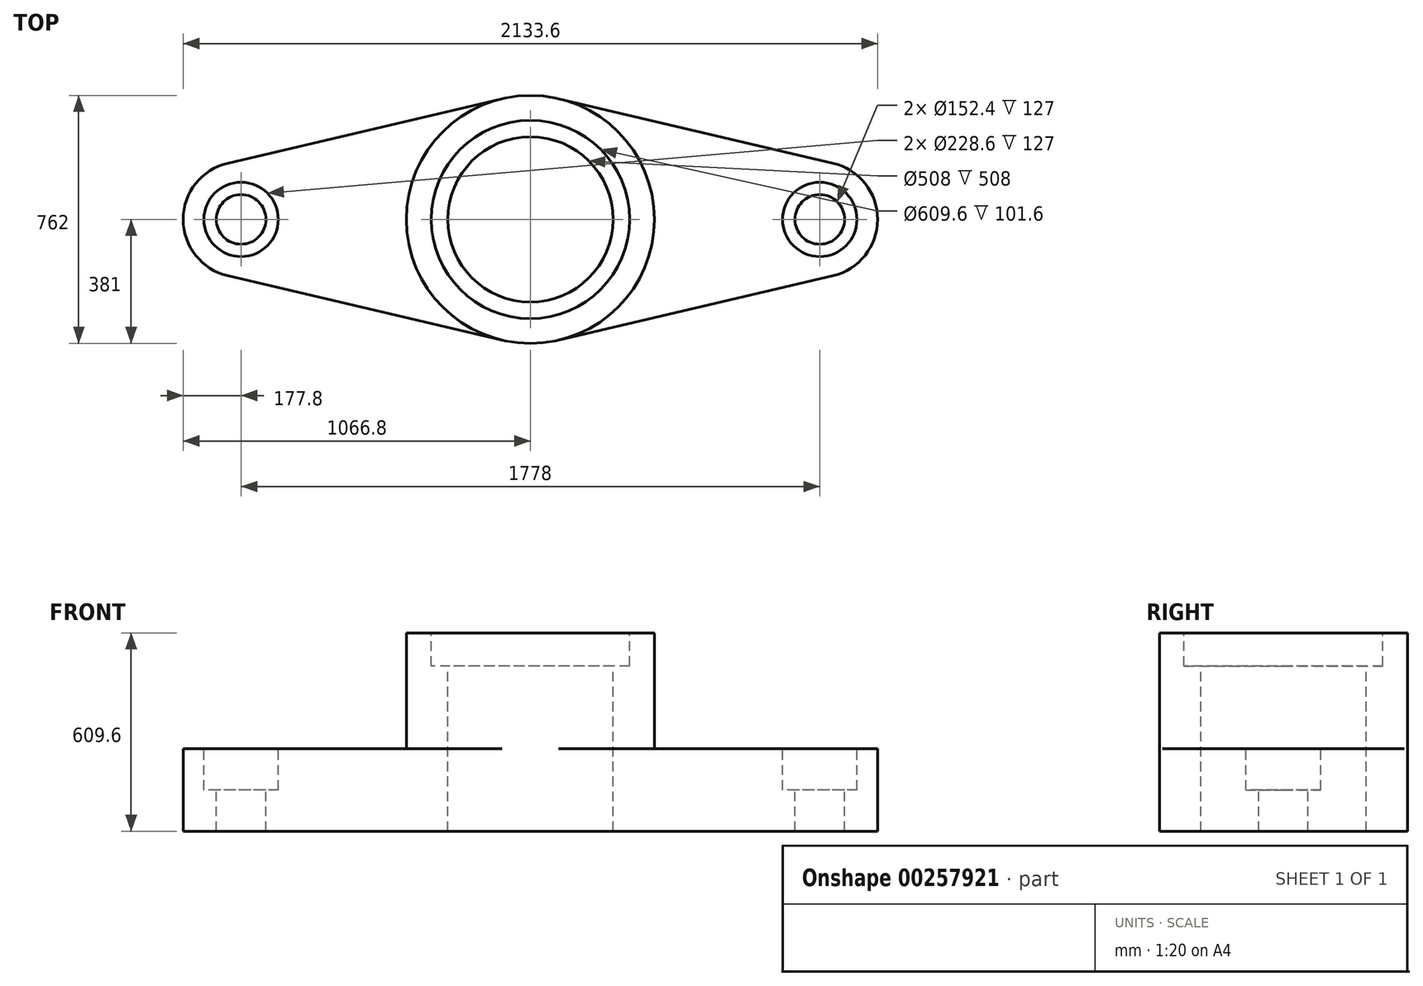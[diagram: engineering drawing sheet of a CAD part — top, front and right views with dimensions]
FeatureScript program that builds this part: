
annotation { "Feature Type Name" : "Feature", "Feature Type Description" : "" }
export const myFeature = defineFeature(function(context is Context, id is Id, definition is map)
    precondition{}
    {
        {
            var Q0;
            Q0=qCreatedBy(makeId("Top.planeOp"),FACE);
            var sketch = newSketch(context, id + "F0", { "sketchPlane" : qUnion([Q0])});
            skCircle(sketch, "E0", {"center": v(0, 0) * mm, "radius": 381 * mm});
            skLineSegment(sketch, "E1", {"start": v(-658.77, 0) * mm, "end": v(889.36, 0) * mm, "construction": true});
            skArc(sketch, "E2", {"start": v(-929.64, 173.1) * mm, "mid": v(-1066.8, 0) * mm, "end": v(-929.64, -173.1) * mm});
            skLineSegment(sketch, "E3", {"start": v(0, 868.24) * mm, "end": v(0, -595.44) * mm, "construction": true});
            skArc(sketch, "E4.MirrorC", {"start": v(929.64, 173.1) * mm, "mid": v(1066.8, 0) * mm, "end": v(929.64, -173.1) * mm});
            skLineSegment(sketch, "E5", {"start": v(-87.09, -370.91) * mm, "end": v(-929.64, -173.1) * mm});
            skLineSegment(sketch, "E6", {"start": v(-87.09, 370.91) * mm, "end": v(-929.64, 173.1) * mm});
            skLineSegment(sketch, "E7.MirrorCS", {"start": v(87.09, 370.91) * mm, "end": v(929.64, 173.1) * mm});
            skLineSegment(sketch, "E8.MirrorCS", {"start": v(87.09, -370.91) * mm, "end": v(929.64, -173.1) * mm});
            skSolve(sketch);
        }
        {
            var Q0;
            Q0 = qSketchRegion(id + "F0", true);
            extrude(context, id + "F1", {"entities" : qUnion([Q0]), "oppositeDirection" : true, "depth" : 254 * mm});
        }
        {
            var Q0;
            Q0=makeQuery(id+"F1.opExtrude","CAP_FACE",FACE,{"disambiguationData":[OSD([sQuery(id+"F0.wireOp",EDGE,"E0"),sQuery(id+"F0.wireOp",EDGE,"E2"),sQuery(id+"F0.wireOp",EDGE,"E5"),sQuery(id+"F0.wireOp",EDGE,"E6"),sQuery(id+"F0.wireOp",EDGE,"E7.MirrorCS"),sQuery(id+"F0.wireOp",EDGE,"E4.MirrorC"),sQuery(id+"F0.wireOp",EDGE,"E8.MirrorCS")])],"isStart":true});
            var sketch = newSketch(context, id + "F2", { "sketchPlane" : qUnion([Q0])});
            skCircle(sketch, "E9", {"center": v(0, 0) * mm, "radius": 381 * mm});
            skSolve(sketch);
        }
        {
            var Q0;
            Q0 = qSketchRegion(id + "F2", true);
            extrude(context, id + "F3", {"entities" : qUnion([Q0]), "operationType" : NewBodyOperationType.ADD, "depth" : 355.6 * mm});
        }
        {
            var Q0;
            {var subQ0=sQuery(id+"F0.wireOp",EDGE,"E5");var subQ1=sQuery(id+"F0.wireOp",EDGE,"E2");var subQ2=sQuery(id+"F0.wireOp",EDGE,"E0");var subQ3=sQuery(id+"F0.wireOp",EDGE,"E8.MirrorCS");var subQ4=sQuery(id+"F0.wireOp",EDGE,"E6");var subQ5=sQuery(id+"F0.wireOp",EDGE,"E7.MirrorCS");Q0=makeQuery(id+"F3.boolean.opBoolean","SPLIT",FACE,{"disambiguationData":[TD([makeQuery(id+"F1.opExtrude","SWEPT_FACE",FACE,{"disambiguationData":[OSD([subQ1])]})])],"derivedFrom":makeQuery(id+"F1.opExtrude","CAP_FACE",FACE,{"disambiguationData":[OSD([subQ2,subQ1,subQ0,subQ4,subQ5,sQuery(id+"F0.wireOp",EDGE,"E4.MirrorC"),subQ3])],"isStart":true})});}
            var sketch = newSketch(context, id + "F4", { "sketchPlane" : qUnion([Q0])});
            skCircle(sketch, "E10", {"center": v(-889, 0) * mm, "radius": 76.2 * mm});
            skSolve(sketch);
        }
        {
            var Q0;
            Q0 = qSketchRegion(id + "F4", true);
            extrude(context, id + "F5", {"entities" : qUnion([Q0]), "operationType" : NewBodyOperationType.REMOVE, "oppositeDirection" : true, "depth" : 254 * mm});
        }
        {
            var Q0;
            {var subQ0=sQuery(id+"F0.wireOp",EDGE,"E7.MirrorCS");var subQ1=sQuery(id+"F0.wireOp",EDGE,"E4.MirrorC");var subQ2=sQuery(id+"F0.wireOp",EDGE,"E5");var subQ3=sQuery(id+"F0.wireOp",EDGE,"E0");var subQ4=sQuery(id+"F0.wireOp",EDGE,"E8.MirrorCS");var subQ5=sQuery(id+"F0.wireOp",EDGE,"E6");Q0=makeQuery(id+"F3.boolean.opBoolean","SPLIT",FACE,{"disambiguationData":[TD([makeQuery(id+"F1.opExtrude","SWEPT_FACE",FACE,{"disambiguationData":[OSD([subQ0])]})])],"derivedFrom":makeQuery(id+"F1.opExtrude","CAP_FACE",FACE,{"disambiguationData":[OSD([subQ3,sQuery(id+"F0.wireOp",EDGE,"E2"),subQ2,subQ5,subQ0,subQ1,subQ4])],"isStart":true})});}
            var sketch = newSketch(context, id + "F6", { "sketchPlane" : qUnion([Q0])});
            skCircle(sketch, "E11", {"center": v(889, 0) * mm, "radius": 76.2 * mm});
            skSolve(sketch);
        }
        {
            var Q0;
            Q0 = qSketchRegion(id + "F6", true);
            extrude(context, id + "F7", {"entities" : qUnion([Q0]), "operationType" : NewBodyOperationType.REMOVE, "oppositeDirection" : true, "depth" : 254 * mm});
        }
        {
            var Q0;
            {var subQ0=sQuery(id+"F0.wireOp",EDGE,"E5");var subQ1=sQuery(id+"F0.wireOp",EDGE,"E2");var subQ2=sQuery(id+"F0.wireOp",EDGE,"E0");var subQ3=sQuery(id+"F0.wireOp",EDGE,"E8.MirrorCS");var subQ4=sQuery(id+"F0.wireOp",EDGE,"E6");var subQ5=sQuery(id+"F0.wireOp",EDGE,"E7.MirrorCS");Q0=makeQuery(id+"F3.boolean.opBoolean","SPLIT",FACE,{"disambiguationData":[TD([makeQuery(id+"F1.opExtrude","SWEPT_FACE",FACE,{"disambiguationData":[OSD([subQ1])]})])],"derivedFrom":makeQuery(id+"F1.opExtrude","CAP_FACE",FACE,{"disambiguationData":[OSD([subQ2,subQ1,subQ0,subQ4,subQ5,sQuery(id+"F0.wireOp",EDGE,"E4.MirrorC"),subQ3])],"isStart":true})});}
            var sketch = newSketch(context, id + "F8", { "sketchPlane" : qUnion([Q0])});
            skCircle(sketch, "E12", {"center": v(-889, 0) * mm, "radius": 114.3 * mm});
            skSolve(sketch);
        }
        {
            var Q0;
            Q0=makeQuery(id+"F8.imprint","IMPRINT",FACE,{"disambiguationData":[TD([[makeQuery(id+"F8.imprint","IMPRINT",EDGE,{"derivedFrom":sQuery(id+"F8.wireOp",EDGE,"E12")}),1.0]])]});
            extrude(context, id + "F9", {"entities" : qUnion([Q0]), "operationType" : NewBodyOperationType.REMOVE, "oppositeDirection" : true, "depth" : 127 * mm});
        }
        {
            var Q0;
            Q0=makeQuery(id+"F8.imprint","IMPRINT",FACE,{"disambiguationData":[TD([[makeQuery(id+"F8.imprint","IMPRINT",EDGE,{"derivedFrom":sQuery(id+"F8.wireOp",EDGE,"E12")}),1.0]])]});
            extrude(context, id + "F10", {"entities" : qUnion([Q0]), "operationType" : NewBodyOperationType.REMOVE, "oppositeDirection" : true, "depth" : 25.4 * mm});
        }
        {
            var Q0;
            {var subQ0=sQuery(id+"F0.wireOp",EDGE,"E7.MirrorCS");var subQ1=sQuery(id+"F0.wireOp",EDGE,"E4.MirrorC");var subQ2=sQuery(id+"F0.wireOp",EDGE,"E5");var subQ3=sQuery(id+"F0.wireOp",EDGE,"E0");var subQ4=sQuery(id+"F0.wireOp",EDGE,"E8.MirrorCS");var subQ5=sQuery(id+"F0.wireOp",EDGE,"E6");Q0=makeQuery(id+"F3.boolean.opBoolean","SPLIT",FACE,{"disambiguationData":[TD([makeQuery(id+"F1.opExtrude","SWEPT_FACE",FACE,{"disambiguationData":[OSD([subQ0])]})])],"derivedFrom":makeQuery(id+"F1.opExtrude","CAP_FACE",FACE,{"disambiguationData":[OSD([subQ3,sQuery(id+"F0.wireOp",EDGE,"E2"),subQ2,subQ5,subQ0,subQ1,subQ4])],"isStart":true})});}
            var sketch = newSketch(context, id + "F11", { "sketchPlane" : qUnion([Q0])});
            skCircle(sketch, "E13", {"center": v(889, 0) * mm, "radius": 114.3 * mm});
            skSolve(sketch);
        }
        {
            var Q0;
            Q0=makeQuery(id+"F11.imprint","IMPRINT",FACE,{"disambiguationData":[TD([[makeQuery(id+"F11.imprint","IMPRINT",EDGE,{"derivedFrom":sQuery(id+"F11.wireOp",EDGE,"E13")}),1.0]])]});
            extrude(context, id + "F12", {"entities" : qUnion([Q0]), "operationType" : NewBodyOperationType.REMOVE, "oppositeDirection" : true, "depth" : 127 * mm});
        }
        {
            var Q0;
            Q0=makeQuery(id+"F3.opExtrude","CAP_FACE",FACE,{"disambiguationData":[OSD([sQuery(id+"F2.wireOp",EDGE,"E9")])],"isStart":false});
            var sketch = newSketch(context, id + "F13", { "sketchPlane" : qUnion([Q0])});
            skCircle(sketch, "E14", {"center": v(0, 0) * mm, "radius": 254 * mm});
            skSolve(sketch);
        }
        {
            var Q0;
            Q0 = qSketchRegion(id + "F13", true);
            extrude(context, id + "F14", {"entities" : qUnion([Q0]), "operationType" : NewBodyOperationType.REMOVE, "oppositeDirection" : true, "depth" : 609.6 * mm});
        }
        {
            var Q0;
            Q0=makeQuery(id+"F3.opExtrude","CAP_FACE",FACE,{"disambiguationData":[OSD([sQuery(id+"F2.wireOp",EDGE,"E9")])],"isStart":false});
            var sketch = newSketch(context, id + "F15", { "sketchPlane" : qUnion([Q0])});
            skCircle(sketch, "E15", {"center": v(0, 0) * mm, "radius": 304.8 * mm});
            skSolve(sketch);
        }
        {
            var Q0;
            Q0 = qSketchRegion(id + "F15", true);
            extrude(context, id + "F16", {"entities" : qUnion([Q0]), "operationType" : NewBodyOperationType.REMOVE, "oppositeDirection" : true, "depth" : 101.6 * mm});
        }
    });
